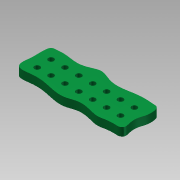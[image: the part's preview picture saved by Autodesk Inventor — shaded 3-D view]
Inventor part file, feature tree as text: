
AUTODESK INVENTOR PART (.ipt)
format: ipt  version: 2011 (Build 150239000, 239)  size: 127,488 bytes
history: native  units: mm
features: extrude x1, sketch x1, reference x1
ambient origin geometry x8: Origin, YZ Plane, XZ Plane, XY Plane, X Axis, Y Axis, Z Axis, Center Point
feature tree (3):
  extrude  "Выдавливание2"  Depth=1.0mm
  sketch  "Эскиз1"
  reference  "Ссылка1"
